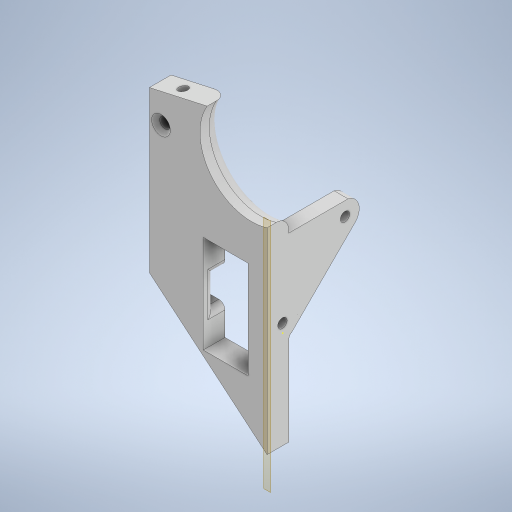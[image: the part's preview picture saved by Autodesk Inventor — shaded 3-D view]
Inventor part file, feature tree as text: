
AUTODESK INVENTOR PART (.ipt)
format: ipt  version: 2023 (Build 270158000, 158)  size: 573,952 bytes
history: native  units: in
note: dims shown in document units (in); Inventor stores cm internally (conversion verified against a paired STEP export)
features: sketch x28, extrude x10, other x9, projected_geometry x9, reference x8, fillet x3, hole x2
ambient origin geometry x8: Origin, YZ Plane, XZ Plane, XY Plane, X Axis, Y Axis, Z Axis, Center Point
bodies: Body1 (feature_tree), Body2 (feature_tree), Body3 (feature_tree)
feature tree (69):
  other  "SCIANA_2.0_MIR.ipt"
  extrude  "Wyciągnięcie proste1"  Depth=0.3937in
  extrude  "Wyciągnięcie proste2"  Depth=0.1772in TaperAngle=0.0deg
  sketch  "Szkic20"
  sketch  "Szkic21"
  extrude  "Wyciągnięcie proste3"  Depth=0.315in TaperAngle=0.0deg
  extrude  "Wyciągnięcie proste4"  Depth=0.315in TaperAngle=0.0deg
  extrude  "Wyciągnięcie proste5"  Depth=0.3937in TaperAngle=0.0deg
  sketch  "Szkic23"
  extrude  "Wyciągnięcie proste6"  TaperAngle=0.0deg  [1 undecoded]
  extrude  "Wyciągnięcie proste7"  Depth=0.3937in TaperAngle=0.0deg
  extrude  "Wyciągnięcie proste8"  Depth=0.3937in TaperAngle=0.0deg
  fillet  "Zaokrąglenie1"  Radius=0.2165in
  fillet  "Zaokrąglenie2"  Radius=0.0827in
  extrude  "Wyciągnięcie proste9"  Depth=0.0787in
  fillet  "Zaokrąglenie4"  Radius=0.0787in
  hole  "Otwór2"  [1 undecoded]
  hole  "Otwór3"  [1 undecoded]
  extrude  "Wyciągnięcie proste10"  Depth=0.2992in
  other  "Bryła1::SCIANA_2.0_MIR.ipt"
  other  "Bryła wyprowadzona1"
  sketch  "Szkic1"
  sketch  "Szkic2"
  sketch  "Szkic3"
  sketch  "Szkic4"
  sketch  "Szkic5"
  sketch  "Szkic6"
  sketch  "Szkic7"
  sketch  "Szkic8"
  sketch  "Szkic9"
  sketch  "Szkic10"
  sketch  "Szkic11"
  sketch  "Szkic12"
  sketch  "Szkic13"
  sketch  "Szkic14"
  sketch  "Szkic15"
  sketch  "Szkic16"
  sketch  "Szkic17"
  other  "Płaszczyzna konstrukcyjna1"
  other  "Płaszczyzna konstrukcyjna2"
  sketch  "Szkic18"
  reference  "Odniesienie1"
  reference  "Odniesienie2"
  projected_geometry  "Pętla rzutowana1"
  reference  "Odniesienie3"
  reference  "Odniesienie4"
  reference  "Odniesienie5"
  reference  "Odniesienie6"
  reference  "Odniesienie7"
  sketch  "Szkic19"
  reference  "Odniesienie8"
  projected_geometry  "Pętla rzutowana2"
  sketch  "Szkic22"
  projected_geometry  "Pętla rzutowana3"
  projected_geometry  "Pętla rzutowana4"
  sketch  "Szkic24"
  projected_geometry  "Pętla rzutowana5"
  sketch  "Szkic26"
  projected_geometry  "Pętla rzutowana7"
  sketch  "Szkic27"
  projected_geometry  "Pętla rzutowana8"
  sketch  "Szkic28"
  projected_geometry  "Pętla rzutowana9"
  sketch  "Szkic29"
  projected_geometry  "Pętla rzutowana10"
  other  "Bryła1"
  other  "<userpath>\Desktop\MojeRoboty\Stefan\mechanics\Zespół1.iam"
  other  "Zespół1.iam"
  other  "sciana_prawa_v4:1"
note: 3 required parameter values undecoded (feature->parameter linkage not recoverable at this tier; creation-order binding heuristic only, values carry confidence <= 0.55)
